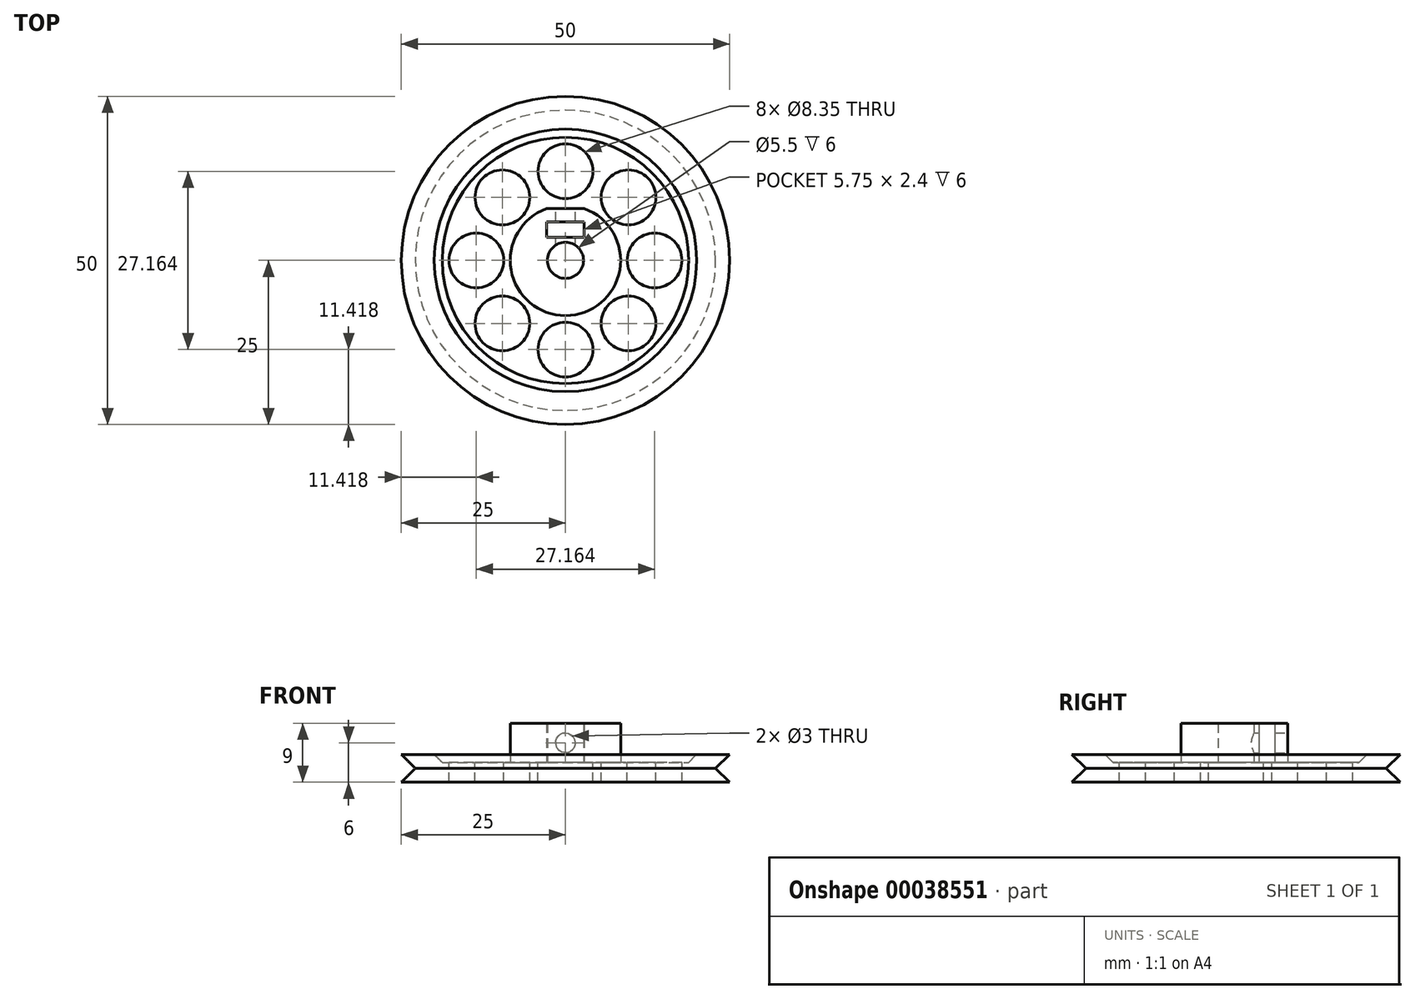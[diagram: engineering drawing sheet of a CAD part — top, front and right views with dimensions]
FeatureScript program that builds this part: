
annotation { "Feature Type Name" : "Feature", "Feature Type Description" : "" }
export const myFeature = defineFeature(function(context is Context, id is Id, definition is map)
    precondition{}
    {
        {
            var Q0;
            Q0=qCreatedBy(makeId("Top.planeOp"),FACE);
            var sketch = newSketch(context, id + "F0", { "sketchPlane" : qUnion([Q0])});
            skCircle(sketch, "E0", {"center": v(0, 0) * mm, "radius": 2.75 * mm});
            skLineSegment(sketch, "E1.bottom", {"start": v(-2.88, 5.9) * mm, "end": v(2.88, 5.9) * mm});
            skLineSegment(sketch, "E1.top", {"start": v(-2.88, 3.5) * mm, "end": v(2.88, 3.5) * mm});
            skLineSegment(sketch, "E1.left", {"start": v(-2.88, 5.9) * mm, "end": v(-2.88, 3.5) * mm});
            skLineSegment(sketch, "E1.right", {"start": v(2.87, 5.9) * mm, "end": v(2.87, 3.5) * mm});
            skPoint(sketch, "E2.positionSnap0", {"position": v(0, 3.5) * mm});
            skArc(sketch, "E3", {"start": v(-2.88, 7.9) * mm, "mid": v(0, -8.4) * mm, "end": v(2.88, 7.9) * mm});
            skLineSegment(sketch, "E4", {"start": v(-2.88, 7.9) * mm, "end": v(2.88, 7.9) * mm});
            skSolve(sketch);
        }
        {
            var Q0;
            Q0 = qSketchRegion(id + "F0", true);
            extrude(context, id + "F1", {"entities" : qUnion([Q0]), "depth" : 7 * mm});
        }
        {
            var Q0;
            Q0=qCreatedBy(makeId("Front.planeOp"),FACE);
            var sketch = newSketch(context, id + "F2", { "sketchPlane" : qUnion([Q0])});
            skLineSegment(sketch, "E5", {"start": v(0, 0) * mm, "end": v(0, 1) * mm});
            skLineSegment(sketch, "E6", {"start": v(0, 1) * mm, "end": v(18.76, 1) * mm});
            skLineSegment(sketch, "E7", {"start": v(18.76, 1) * mm, "end": v(20, 2.24) * mm});
            skLineSegment(sketch, "E8", {"start": v(20, 2.24) * mm, "end": v(25, 2.24) * mm});
            skLineSegment(sketch, "E9", {"start": v(25, 2.24) * mm, "end": v(22.88, 0.12) * mm});
            skLineSegment(sketch, "E10", {"start": v(22.88, 0.12) * mm, "end": v(25, -2) * mm});
            skLineSegment(sketch, "E11", {"start": v(25, -2) * mm, "end": v(0, -2) * mm});
            skLineSegment(sketch, "E12", {"start": v(0, -2) * mm, "end": v(0, 0) * mm});
            skCircle(sketch, "E13", {"center": v(25, 0.12) * mm, "radius": 1.5 * mm, "construction": true});
            skSolve(sketch);
        }
        {
            var Q0;
            Q0=makeQuery(id+"F2.imprint","IMPRINT",FACE,{"disambiguationData":[TD([[makeQuery(id+"F2.imprint","IMPRINT",EDGE,{"derivedFrom":sQuery(id+"F2.wireOp",EDGE,"E5")}),-1.0]])]});
            var Q1;
            Q1=sQuery(id+"F2.wireOp",EDGE,"E12");
            revolve(context, id + "F3", {"operationType" : NewBodyOperationType.ADD, "entities" : qUnion([Q0]), "axis" : qUnion([Q1]), "revolveType" : RevolveType.FULL});
        }
        {
            var Q0;
            Q0=makeQuery(id+"F3.boolean.opBoolean","SPLIT",FACE,{"disambiguationData":[TD([makeQuery(id+"F1.opExtrude","SWEPT_FACE",FACE,{"disambiguationData":[OSD([sQuery(id+"F0.wireOp",EDGE,"E3")])]})])],"derivedFrom":makeQuery(id+"F3.opRevolve","SWEPT_FACE",FACE,{"disambiguationData":[OSD([sQuery(id+"F2.wireOp",EDGE,"E6")])]})});
            var sketch = newSketch(context, id + "F4", { "sketchPlane" : qUnion([Q0])});
            skCircle(sketch, "E14", {"center": v(0, 0) * mm, "radius": 9.4 * mm, "construction": true});
            skCircle(sketch, "E15", {"center": v(0, 0) * mm, "radius": 17.76 * mm, "construction": true});
            skCircle(sketch, "E16", {"center": v(13.58, 0) * mm, "radius": 4.18 * mm});
            skLineSegment(sketch, "E17", {"start": v(25, 0) * mm, "end": v(-25, 0) * mm, "construction": true});
            skLineSegment(sketch, "E18", {"start": v(0, -25) * mm, "end": v(0, 25) * mm, "construction": true});
            skPoint(sketch, "E18.startSnap0", {"position": v(0, -8.4) * mm});
            skPoint(sketch, "E18.endSnap0", {"position": v(0, 7.9) * mm});
            skLineSegment(sketch, "E19", {"start": v(-17.68, 17.68) * mm, "end": v(17.68, -17.68) * mm, "construction": true});
            skLineSegment(sketch, "E20", {"start": v(17.68, 17.68) * mm, "end": v(-17.68, -17.68) * mm, "construction": true});
            skCircle(sketch, "E21", {"center": v(9.6, -9.6) * mm, "radius": 4.18 * mm});
            skCircle(sketch, "E22", {"center": v(0, -13.58) * mm, "radius": 4.18 * mm});
            skCircle(sketch, "E23", {"center": v(-9.6, -9.6) * mm, "radius": 4.18 * mm});
            skCircle(sketch, "E24", {"center": v(-13.58, 0) * mm, "radius": 4.18 * mm});
            skCircle(sketch, "E25", {"center": v(-9.6, 9.6) * mm, "radius": 4.18 * mm});
            skCircle(sketch, "E26", {"center": v(0, 13.58) * mm, "radius": 4.18 * mm});
            skCircle(sketch, "E27", {"center": v(9.6, 9.6) * mm, "radius": 4.18 * mm});
            skSolve(sketch);
        }
        {
            var Q0;
            Q0 = qSketchRegion(id + "F4", true);
            extrude(context, id + "F5", {"entities" : qUnion([Q0]), "operationType" : NewBodyOperationType.REMOVE, "endBound" : BoundingType.THROUGH_ALL, "oppositeDirection" : true, "depth" : 25 * mm});
        }
        {
            var Q0;
            Q0=makeQuery(id+"F1.opExtrude","SWEPT_FACE",FACE,{"disambiguationData":[OSD([sQuery(id+"F0.wireOp",EDGE,"E4")])]});
            var sketch = newSketch(context, id + "F6", { "sketchPlane" : qUnion([Q0])});
            skLineSegment(sketch, "E28", {"start": v(2.87, 7) * mm, "end": v(-2.87, 1) * mm, "construction": true});
            skCircle(sketch, "E29", {"center": v(0, 4) * mm, "radius": 1.5 * mm});
            skSolve(sketch);
        }
        {
            var Q0;
            Q0 = qSketchRegion(id + "F6", true);
            var Q1;
            Q1=makeQuery(id+"F1.opExtrude","SWEPT_FACE",FACE,{"disambiguationData":[OSD([sQuery(id+"F0.wireOp",EDGE,"E0")])]});
            extrude(context, id + "F7", {"entities" : qUnion([Q0]), "operationType" : NewBodyOperationType.REMOVE, "endBound" : BoundingType.UP_TO_SURFACE, "oppositeDirection" : true, "endBoundEntityFace" : qUnion([Q1]), "depth" : 25 * mm});
        }
    });
